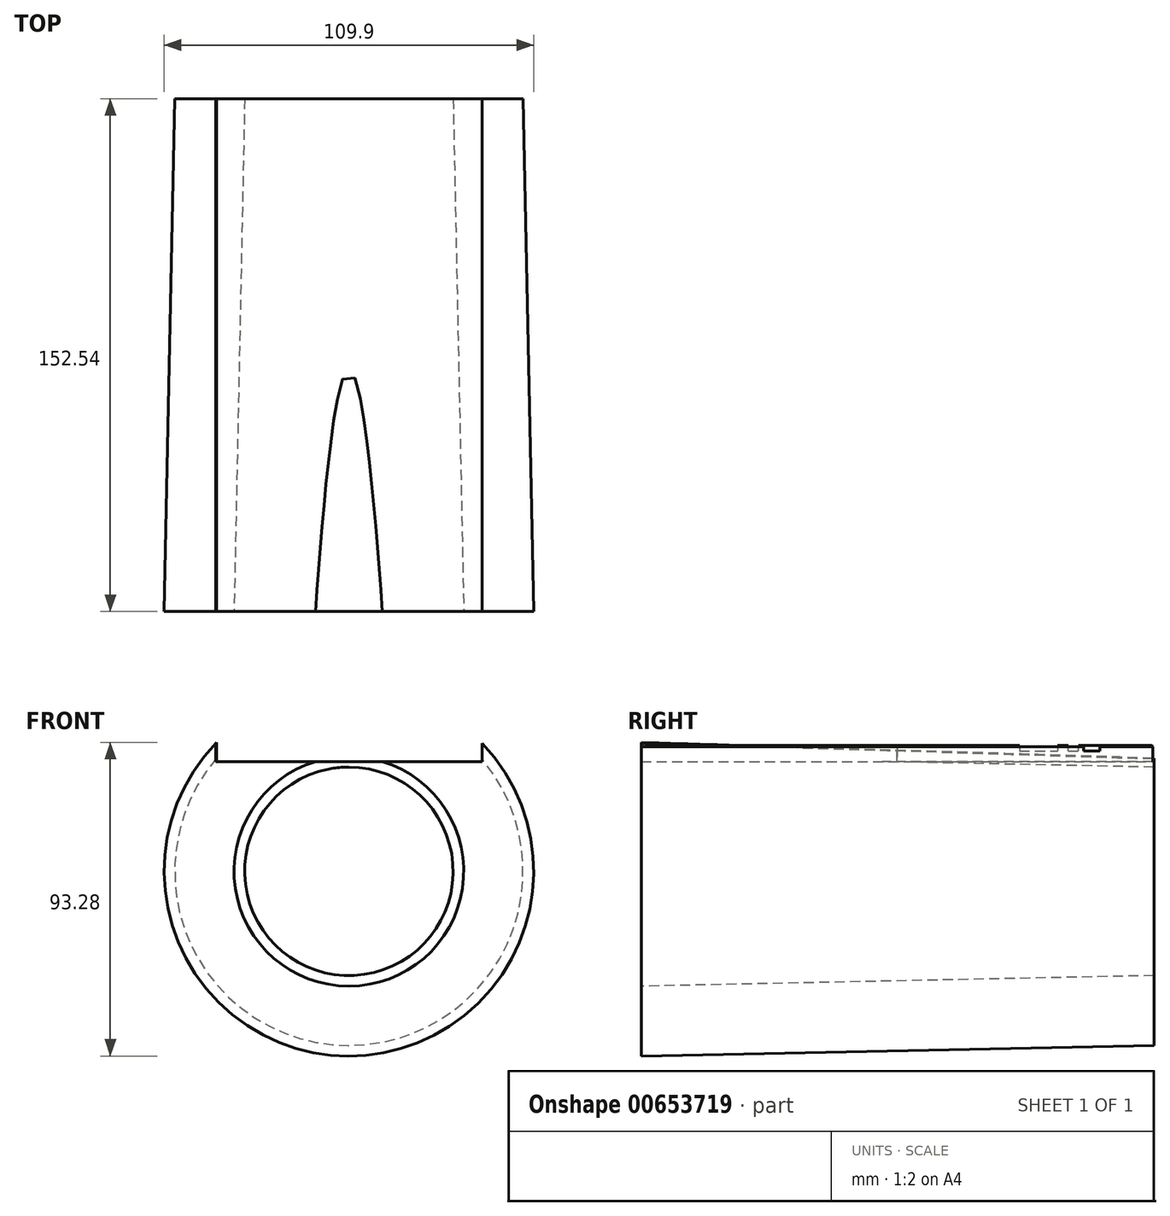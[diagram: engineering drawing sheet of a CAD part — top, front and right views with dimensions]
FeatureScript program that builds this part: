
annotation { "Feature Type Name" : "Feature", "Feature Type Description" : "" }
export const myFeature = defineFeature(function(context is Context, id is Id, definition is map)
    precondition{}
    {
        {
            var Q0;
            Q0=qCreatedBy(makeId("Top.planeOp"),FACE);
            var sketch = newSketch(context, id + "F0", { "sketchPlane" : qUnion([Q0])});
            skLineSegment(sketch, "E0.bottom", {"start": v(-25.4, 66.66) * mm, "end": v(-15.87, 66.66) * mm});
            skLineSegment(sketch, "E0.top", {"start": v(-26.98, 62.7) * mm, "end": v(-17.45, 62.7) * mm});
            skLineSegment(sketch, "E0.left", {"start": v(-26.98, 65.07) * mm, "end": v(-26.98, 62.7) * mm});
            skLineSegment(sketch, "E0.right", {"start": v(-15.87, 66.66) * mm, "end": v(-15.87, 64.28) * mm});
            skArc(sketch, "E1.filletArc", {"start": v(-25.4, 66.66) * mm, "mid": v(-26.51, 66.2) * mm, "end": v(-26.98, 65.07) * mm});
            skArc(sketch, "E2.filletArc", {"start": v(-17.45, 62.7) * mm, "mid": v(-16.33, 63.16) * mm, "end": v(-15.87, 64.28) * mm});
            skLineSegment(sketch, "E3.bottom", {"start": v(-34.92, 50.83) * mm, "end": v(-33.34, 50.83) * mm});
            skLineSegment(sketch, "E3.top", {"start": v(-34.92, 54) * mm, "end": v(-33.34, 54) * mm});
            skLineSegment(sketch, "E4.bottom", {"start": v(-34.92, 47.66) * mm, "end": v(-33.34, 47.66) * mm});
            skLineSegment(sketch, "E4.top", {"start": v(-34.92, 36.55) * mm, "end": v(-33.34, 36.55) * mm});
            skLineSegment(sketch, "E5.bottom", {"start": v(34.92, 60.29) * mm, "end": v(33.33, 60.29) * mm});
            skLineSegment(sketch, "E5.top", {"start": v(34.92, 55.52) * mm, "end": v(33.33, 55.52) * mm});
            skLineSegment(sketch, "E6.bottom", {"start": v(26.99, -69.85) * mm, "end": v(-26.99, -69.85) * mm});
            skLineSegment(sketch, "E6.top", {"start": v(26.99, 69.85) * mm, "end": v(-26.99, 69.85) * mm});
            skLineSegment(sketch, "E6.left", {"start": v(33.34, -63.5) * mm, "end": v(33.34, 63.5) * mm});
            skLineSegment(sketch, "E6.right", {"start": v(-33.34, -63.5) * mm, "end": v(-33.34, 63.5) * mm});
            skPoint(sketch, "E6.middle", {"position": v(0, 0) * mm});
            skLineSegment(sketch, "E7.bottom", {"start": v(28.57, 71.42) * mm, "end": v(-28.57, 71.42) * mm});
            skLineSegment(sketch, "E7.top", {"start": v(28.57, -71.42) * mm, "end": v(-28.57, -71.42) * mm});
            skLineSegment(sketch, "E7.left", {"start": v(34.92, 65.07) * mm, "end": v(34.92, -65.07) * mm});
            skLineSegment(sketch, "E7.right", {"start": v(-34.92, 65.07) * mm, "end": v(-34.92, -65.07) * mm});
            skLineSegment(sketch, "E8.bottom", {"start": v(24.6, -67.47) * mm, "end": v(-24.6, -67.47) * mm});
            skLineSegment(sketch, "E8.top", {"start": v(24.6, 67.47) * mm, "end": v(-24.6, 67.47) * mm});
            skLineSegment(sketch, "E8.left", {"start": v(30.96, -61.12) * mm, "end": v(30.96, 61.12) * mm});
            skLineSegment(sketch, "E8.right", {"start": v(-30.96, -61.12) * mm, "end": v(-30.96, 61.12) * mm});
            skPoint(sketch, "E9.visualSharp", {"position": v(-30.96, -67.47) * mm});
            skPoint(sketch, "E10.visualSharp", {"position": v(30.96, -67.47) * mm});
            skPoint(sketch, "E11.visualSharp", {"position": v(33.34, -69.85) * mm});
            skPoint(sketch, "E12.visualSharp", {"position": v(-33.34, -69.85) * mm});
            skPoint(sketch, "E13.visualSharp", {"position": v(-34.92, -71.42) * mm});
            skPoint(sketch, "E14.visualSharp", {"position": v(34.92, -71.42) * mm});
            skPoint(sketch, "E15.visualSharp", {"position": v(-34.92, 71.42) * mm});
            skPoint(sketch, "E16.visualSharp", {"position": v(-33.34, 69.85) * mm});
            skPoint(sketch, "E17.visualSharp", {"position": v(-30.96, 67.47) * mm});
            skPoint(sketch, "E18.visualSharp", {"position": v(30.96, 67.47) * mm});
            skPoint(sketch, "E19.visualSharp", {"position": v(33.34, 69.85) * mm});
            skPoint(sketch, "E20.visualSharp", {"position": v(34.92, 71.42) * mm});
            skLineSegment(sketch, "E21", {"start": v(-28.57, -71.42) * mm, "end": v(28.57, -71.42) * mm});
            skLineSegment(sketch, "E22.bottom", {"start": v(-25.4, -71.42) * mm, "end": v(-9.52, -71.42) * mm});
            skLineSegment(sketch, "E22.top", {"start": v(-25.4, -69.85) * mm, "end": v(-9.52, -69.85) * mm});
            skLineSegment(sketch, "E22.left", {"start": v(-25.4, -71.42) * mm, "end": v(-25.4, -69.85) * mm});
            skLineSegment(sketch, "E22.right", {"start": v(-9.52, -71.42) * mm, "end": v(-9.52, -69.85) * mm});
            skLineSegment(sketch, "E23.bottom", {"start": v(-4.76, -71.42) * mm, "end": v(6.36, -71.42) * mm});
            skLineSegment(sketch, "E23.top", {"start": v(-4.76, -69.85) * mm, "end": v(6.36, -69.85) * mm});
            skLineSegment(sketch, "E23.left", {"start": v(-4.76, -71.42) * mm, "end": v(-4.76, -69.85) * mm});
            skLineSegment(sketch, "E23.right", {"start": v(6.36, -71.42) * mm, "end": v(6.36, -69.85) * mm});
            skLineSegment(sketch, "E24", {"start": v(-28.57, -71.42) * mm, "end": v(12.42, -71.42) * mm});
            skLineSegment(sketch, "E25", {"start": v(-28.57, -71.42) * mm, "end": v(11.12, -71.42) * mm});
            skLineSegment(sketch, "E26.bottom", {"start": v(11.12, -71.42) * mm, "end": v(27.4, -71.42) * mm});
            skLineSegment(sketch, "E26.top", {"start": v(11.12, -69.85) * mm, "end": v(27.4, -69.85) * mm});
            skLineSegment(sketch, "E26.left", {"start": v(11.12, -71.42) * mm, "end": v(11.12, -69.85) * mm});
            skLineSegment(sketch, "E26.right", {"start": v(27.4, -71.42) * mm, "end": v(27.4, -69.85) * mm});
            skLineSegment(sketch, "E27", {"start": v(-24.6, -67.47) * mm, "end": v(24.6, -67.47) * mm});
            skLineSegment(sketch, "E28", {"start": v(-33.34, 63.5) * mm, "end": v(-33.34, -63.5) * mm});
            skLineSegment(sketch, "E29", {"start": v(-26.99, -69.85) * mm, "end": v(27.4, -69.85) * mm});
            skLineSegment(sketch, "E30", {"start": v(33.34, -69.85) * mm, "end": v(33.34, -69.27) * mm});
            skLineSegment(sketch, "E31", {"start": v(-28.57, 71.42) * mm, "end": v(28.57, 71.42) * mm});
            skLineSegment(sketch, "E32", {"start": v(34.92, -65.07) * mm, "end": v(34.92, 65.07) * mm});
            skLineSegment(sketch, "E33", {"start": v(-34.92, -65.07) * mm, "end": v(-34.92, 65.07) * mm});
            skArc(sketch, "E34.filletArc", {"start": v(-30.96, -61.12) * mm, "mid": v(-29.1, -65.6) * mm, "end": v(-24.6, -67.47) * mm});
            skArc(sketch, "E35.filletArc", {"start": v(-33.34, -63.5) * mm, "mid": v(-31.48, -68) * mm, "end": v(-26.99, -69.85) * mm});
            skArc(sketch, "E36.filletArc", {"start": v(-34.92, -65.07) * mm, "mid": v(-33.06, -69.56) * mm, "end": v(-28.57, -71.42) * mm});
            skArc(sketch, "E37.filletArc", {"start": v(28.57, -71.42) * mm, "mid": v(33.06, -69.56) * mm, "end": v(34.92, -65.07) * mm});
            skArc(sketch, "E38.filletArc", {"start": v(26.99, -69.85) * mm, "mid": v(31.48, -68) * mm, "end": v(33.34, -63.5) * mm});
            skArc(sketch, "E39.filletArc", {"start": v(24.6, -67.47) * mm, "mid": v(29.1, -65.6) * mm, "end": v(30.96, -61.12) * mm});
            skArc(sketch, "E40.filletArc", {"start": v(-24.6, 67.47) * mm, "mid": v(-29.1, 65.6) * mm, "end": v(-30.96, 61.12) * mm});
            skArc(sketch, "E41.filletArc", {"start": v(-26.99, 69.85) * mm, "mid": v(-31.48, 68) * mm, "end": v(-33.34, 63.5) * mm});
            skArc(sketch, "E42.filletArc", {"start": v(-28.57, 71.42) * mm, "mid": v(-33.06, 69.56) * mm, "end": v(-34.92, 65.07) * mm});
            skArc(sketch, "E43.filletArc", {"start": v(34.92, 65.07) * mm, "mid": v(33.06, 69.56) * mm, "end": v(28.57, 71.42) * mm});
            skArc(sketch, "E44.filletArc", {"start": v(33.34, 63.5) * mm, "mid": v(31.48, 68) * mm, "end": v(26.99, 69.85) * mm});
            skArc(sketch, "E45.filletArc", {"start": v(30.96, 61.12) * mm, "mid": v(29.1, 65.6) * mm, "end": v(24.6, 67.47) * mm});
            skLineSegment(sketch, "E46.trimOffspring", {"start": v(32.75, -69.85) * mm, "end": v(33.34, -69.85) * mm});
            skSolve(sketch);
        }
        {
            var Q0;
            Q0=makeQuery(id+"F0.imprint","IMPRINT",FACE,{"disambiguationData":[TD([[makeQuery(id+"F0.imprint","IMPRINT",EDGE,{"derivedFrom":sQuery(id+"F0.wireOp",EDGE,"E0.bottom")}),1.0]])]});
            var Q1;
            Q1=makeQuery(id+"F0.imprint","IMPRINT",FACE,{"disambiguationData":[TD([[makeQuery(id+"F0.imprint","IMPRINT",EDGE,{"derivedFrom":sQuery(id+"F0.wireOp",EDGE,"E8.right")}),1.0]])]});
            var Q2;
            {var subQ0=sQuery(id+"F0.wireOp",EDGE,"E28");var subQ1=sQuery(id+"F0.wireOp",EDGE,"E3.bottom");var subQ2=makeQuery(id+"F0.imprint","INTERSECT",VERTEX,{"derivedFrom":[subQ1,subQ0]});Q2=makeQuery(id+"F0.imprint","IMPRINT",FACE,{"disambiguationData":[TD([[makeQuery(id+"F0.imprint","IMPRINT",EDGE,{"disambiguationData":[TD([[subQ2,1.0]])],"derivedFrom":subQ1}),1.0]])]});}
            var Q3;
            {var subQ0=sQuery(id+"F0.wireOp",EDGE,"E28");var subQ1=sQuery(id+"F0.wireOp",EDGE,"E3.bottom");var subQ2=makeQuery(id+"F0.imprint","INTERSECT",VERTEX,{"derivedFrom":[subQ1,subQ0]});Q3=makeQuery(id+"F0.imprint","IMPRINT",FACE,{"disambiguationData":[TD([[makeQuery(id+"F0.imprint","IMPRINT",EDGE,{"disambiguationData":[TD([[subQ2,1.0]])],"derivedFrom":subQ1}),-1.0]])]});}
            var Q4;
            {var subQ0=sQuery(id+"F0.wireOp",EDGE,"E28");var subQ1=sQuery(id+"F0.wireOp",EDGE,"E4.bottom");var subQ2=makeQuery(id+"F0.imprint","INTERSECT",VERTEX,{"derivedFrom":[subQ1,subQ0]});Q4=makeQuery(id+"F0.imprint","IMPRINT",FACE,{"disambiguationData":[TD([[makeQuery(id+"F0.imprint","IMPRINT",EDGE,{"disambiguationData":[TD([[subQ2,1.0]])],"derivedFrom":subQ1}),-1.0]])]});}
            var Q5;
            Q5=makeQuery(id+"F0.imprint","IMPRINT",FACE,{"disambiguationData":[TD([[makeQuery(id+"F0.imprint","IMPRINT",EDGE,{"derivedFrom":sQuery(id+"F0.wireOp",EDGE,"E6.top")}),-1.0]])]});
            var Q6;
            {var subQ5=sQuery(id+"F0.wireOp",EDGE,"E22.left");Q6=makeQuery(id+"F0.imprint","IMPRINT",FACE,{"disambiguationData":[TD([[makeQuery(id+"F0.imprint","IMPRINT",EDGE,{"derivedFrom":subQ5}),1.0]])]});}
            var Q7;
            {var subQ0=sQuery(id+"F0.wireOp",EDGE,"E32");var subQ1=sQuery(id+"F0.wireOp",EDGE,"E5.bottom");var subQ2=makeQuery(id+"F0.imprint","INTERSECT",VERTEX,{"derivedFrom":[subQ1,subQ0]});Q7=makeQuery(id+"F0.imprint","IMPRINT",FACE,{"disambiguationData":[TD([[makeQuery(id+"F0.imprint","IMPRINT",EDGE,{"disambiguationData":[TD([[subQ2,-1.0]])],"derivedFrom":subQ1}),1.0]])]});}
            var Q8;
            {var subQ3=sQuery(id+"F0.wireOp",EDGE,"E21");Q8=makeQuery(id+"F0.imprint","IMPRINT",FACE,{"disambiguationData":[TD([[makeQuery(id+"F0.imprint","IMPRINT",EDGE,{"derivedFrom":subQ3}),1.0]])]});}
            var Q9;
            {var subQ2=sQuery(id+"F0.wireOp",EDGE,"E26.left");Q9=makeQuery(id+"F0.imprint","IMPRINT",FACE,{"disambiguationData":[TD([[makeQuery(id+"F0.imprint","IMPRINT",EDGE,{"derivedFrom":subQ2}),-1.0]])]});}
            var Q10;
            {var subQ0=sQuery(id+"F0.wireOp",EDGE,"E23.right");Q10=makeQuery(id+"F0.imprint","IMPRINT",FACE,{"disambiguationData":[TD([[makeQuery(id+"F0.imprint","IMPRINT",EDGE,{"derivedFrom":subQ0}),-1.0]])]});}
            var Q11;
            {var subQ0=sQuery(id+"F0.wireOp",EDGE,"E23.left");Q11=makeQuery(id+"F0.imprint","IMPRINT",FACE,{"disambiguationData":[TD([[makeQuery(id+"F0.imprint","IMPRINT",EDGE,{"derivedFrom":subQ0}),-1.0]])]});}
            var Q12;
            {var subQ0=sQuery(id+"F0.wireOp",EDGE,"E22.right");Q12=makeQuery(id+"F0.imprint","IMPRINT",FACE,{"disambiguationData":[TD([[makeQuery(id+"F0.imprint","IMPRINT",EDGE,{"derivedFrom":subQ0}),-1.0]])]});}
            var Q13;
            {var subQ0=sQuery(id+"F0.wireOp",EDGE,"E22.left");Q13=makeQuery(id+"F0.imprint","IMPRINT",FACE,{"disambiguationData":[TD([[makeQuery(id+"F0.imprint","IMPRINT",EDGE,{"derivedFrom":subQ0}),-1.0]])]});}
            extrude(context, id + "F1", {"entities" : qUnion([Q0, Q1, Q2, Q3, Q4, Q5, Q6, Q7, Q8, Q9, Q10, Q11, Q12, Q13]), "depth" : 3.17 * mm, "offsetDistance" : 25.4 * mm});
        }
        {
            var Q0;
            {var subQ5=sQuery(id+"F0.wireOp",EDGE,"E22.left");Q0=makeQuery(id+"F0.imprint","IMPRINT",FACE,{"disambiguationData":[TD([[makeQuery(id+"F0.imprint","IMPRINT",EDGE,{"derivedFrom":subQ5}),1.0]])]});}
            var Q1;
            {var subQ0=sQuery(id+"F0.wireOp",EDGE,"E28");var subQ1=sQuery(id+"F0.wireOp",EDGE,"E3.bottom");var subQ2=makeQuery(id+"F0.imprint","INTERSECT",VERTEX,{"derivedFrom":[subQ1,subQ0]});Q1=makeQuery(id+"F0.imprint","IMPRINT",FACE,{"disambiguationData":[TD([[makeQuery(id+"F0.imprint","IMPRINT",EDGE,{"disambiguationData":[TD([[subQ2,1.0]])],"derivedFrom":subQ1}),-1.0]])]});}
            var Q2;
            Q2=makeQuery(id+"F0.imprint","IMPRINT",FACE,{"disambiguationData":[TD([[makeQuery(id+"F0.imprint","IMPRINT",EDGE,{"derivedFrom":sQuery(id+"F0.wireOp",EDGE,"E6.top")}),-1.0]])]});
            var Q3;
            {var subQ3=sQuery(id+"F0.wireOp",EDGE,"E21");Q3=makeQuery(id+"F0.imprint","IMPRINT",FACE,{"disambiguationData":[TD([[makeQuery(id+"F0.imprint","IMPRINT",EDGE,{"derivedFrom":subQ3}),1.0]])]});}
            var Q4;
            {var subQ0=sQuery(id+"F0.wireOp",EDGE,"E22.right");Q4=makeQuery(id+"F0.imprint","IMPRINT",FACE,{"disambiguationData":[TD([[makeQuery(id+"F0.imprint","IMPRINT",EDGE,{"derivedFrom":subQ0}),-1.0]])]});}
            var Q5;
            {var subQ0=sQuery(id+"F0.wireOp",EDGE,"E23.right");Q5=makeQuery(id+"F0.imprint","IMPRINT",FACE,{"disambiguationData":[TD([[makeQuery(id+"F0.imprint","IMPRINT",EDGE,{"derivedFrom":subQ0}),-1.0]])]});}
            extrude(context, id + "F2", {"entities" : qUnion([Q0, Q1, Q2, Q3, Q4, Q5]), "operationType" : NewBodyOperationType.ADD, "depth" : 9.52 * mm, "offsetDistance" : 25.4 * mm});
        }
        {
            var Q0;
            Q0=makeQuery(id+"F0.imprint","IMPRINT",FACE,{"disambiguationData":[TD([[makeQuery(id+"F0.imprint","IMPRINT",EDGE,{"derivedFrom":sQuery(id+"F0.wireOp",EDGE,"E8.right")}),1.0]])]});
            var Q1;
            {var subQ0=sQuery(id+"F0.wireOp",EDGE,"E28");var subQ1=sQuery(id+"F0.wireOp",EDGE,"E4.bottom");var subQ2=makeQuery(id+"F0.imprint","INTERSECT",VERTEX,{"derivedFrom":[subQ1,subQ0]});Q1=makeQuery(id+"F0.imprint","IMPRINT",FACE,{"disambiguationData":[TD([[makeQuery(id+"F0.imprint","IMPRINT",EDGE,{"disambiguationData":[TD([[subQ2,1.0]])],"derivedFrom":subQ1}),-1.0]])]});}
            var Q2;
            {var subQ0=sQuery(id+"F0.wireOp",EDGE,"E28");var subQ1=sQuery(id+"F0.wireOp",EDGE,"E3.bottom");var subQ2=makeQuery(id+"F0.imprint","INTERSECT",VERTEX,{"derivedFrom":[subQ1,subQ0]});Q2=makeQuery(id+"F0.imprint","IMPRINT",FACE,{"disambiguationData":[TD([[makeQuery(id+"F0.imprint","IMPRINT",EDGE,{"disambiguationData":[TD([[subQ2,1.0]])],"derivedFrom":subQ1}),-1.0]])]});}
            var Q3;
            {var subQ0=sQuery(id+"F0.wireOp",EDGE,"E28");var subQ1=sQuery(id+"F0.wireOp",EDGE,"E3.bottom");var subQ2=makeQuery(id+"F0.imprint","INTERSECT",VERTEX,{"derivedFrom":[subQ1,subQ0]});Q3=makeQuery(id+"F0.imprint","IMPRINT",FACE,{"disambiguationData":[TD([[makeQuery(id+"F0.imprint","IMPRINT",EDGE,{"disambiguationData":[TD([[subQ2,1.0]])],"derivedFrom":subQ1}),1.0]])]});}
            var Q4;
            Q4=makeQuery(id+"F0.imprint","IMPRINT",FACE,{"disambiguationData":[TD([[makeQuery(id+"F0.imprint","IMPRINT",EDGE,{"derivedFrom":sQuery(id+"F0.wireOp",EDGE,"E6.top")}),-1.0]])]});
            var Q5;
            {var subQ5=sQuery(id+"F0.wireOp",EDGE,"E22.left");Q5=makeQuery(id+"F0.imprint","IMPRINT",FACE,{"disambiguationData":[TD([[makeQuery(id+"F0.imprint","IMPRINT",EDGE,{"derivedFrom":subQ5}),1.0]])]});}
            var Q6;
            {var subQ0=sQuery(id+"F0.wireOp",EDGE,"E32");var subQ1=sQuery(id+"F0.wireOp",EDGE,"E5.bottom");var subQ2=makeQuery(id+"F0.imprint","INTERSECT",VERTEX,{"derivedFrom":[subQ1,subQ0]});Q6=makeQuery(id+"F0.imprint","IMPRINT",FACE,{"disambiguationData":[TD([[makeQuery(id+"F0.imprint","IMPRINT",EDGE,{"disambiguationData":[TD([[subQ2,-1.0]])],"derivedFrom":subQ1}),1.0]])]});}
            var Q7;
            {var subQ3=sQuery(id+"F0.wireOp",EDGE,"E21");Q7=makeQuery(id+"F0.imprint","IMPRINT",FACE,{"disambiguationData":[TD([[makeQuery(id+"F0.imprint","IMPRINT",EDGE,{"derivedFrom":subQ3}),1.0]])]});}
            var Q8;
            {var subQ0=sQuery(id+"F0.wireOp",EDGE,"E22.left");Q8=makeQuery(id+"F0.imprint","IMPRINT",FACE,{"disambiguationData":[TD([[makeQuery(id+"F0.imprint","IMPRINT",EDGE,{"derivedFrom":subQ0}),-1.0]])]});}
            var Q9;
            {var subQ0=sQuery(id+"F0.wireOp",EDGE,"E22.right");Q9=makeQuery(id+"F0.imprint","IMPRINT",FACE,{"disambiguationData":[TD([[makeQuery(id+"F0.imprint","IMPRINT",EDGE,{"derivedFrom":subQ0}),-1.0]])]});}
            var Q10;
            {var subQ0=sQuery(id+"F0.wireOp",EDGE,"E23.left");Q10=makeQuery(id+"F0.imprint","IMPRINT",FACE,{"disambiguationData":[TD([[makeQuery(id+"F0.imprint","IMPRINT",EDGE,{"derivedFrom":subQ0}),-1.0]])]});}
            var Q11;
            {var subQ0=sQuery(id+"F0.wireOp",EDGE,"E23.right");Q11=makeQuery(id+"F0.imprint","IMPRINT",FACE,{"disambiguationData":[TD([[makeQuery(id+"F0.imprint","IMPRINT",EDGE,{"derivedFrom":subQ0}),-1.0]])]});}
            var Q12;
            {var subQ2=sQuery(id+"F0.wireOp",EDGE,"E26.left");Q12=makeQuery(id+"F0.imprint","IMPRINT",FACE,{"disambiguationData":[TD([[makeQuery(id+"F0.imprint","IMPRINT",EDGE,{"derivedFrom":subQ2}),-1.0]])]});}
            extrude(context, id + "F3", {"entities" : qUnion([Q0, Q1, Q2, Q3, Q4, Q5, Q6, Q7, Q8, Q9, Q10, Q11, Q12]), "depth" : 12.7 * mm, "offsetDistance" : 25.4 * mm, "hasSecondDirection" : true, "secondDirectionOppositeDirection" : false, "secondDirectionDepth" : 9.52 * mm});
        }
        {
            var Q0;
            Q0=makeQuery(id+"F3.opExtrude","CAP_EDGE",EDGE,{"disambiguationData":[OSD([sQuery(id+"F0.wireOp",EDGE,"E32")])],"isStart":false});
            var Q1;
            Q1=makeQuery(id+"F3.opExtrude","CAP_EDGE",EDGE,{"disambiguationData":[OSD([sQuery(id+"F0.wireOp",EDGE,"E37.filletArc")])],"isStart":false});
            var Q2;
            Q2=makeQuery(id+"F3.opExtrude","CAP_EDGE",EDGE,{"disambiguationData":[OSD([sQuery(id+"F0.wireOp",EDGE,"E21"),sQuery(id+"F0.wireOp",EDGE,"E25"),sQuery(id+"F0.wireOp",EDGE,"E26.bottom")])],"isStart":false});
            var Q3;
            Q3=makeQuery(id+"F3.opExtrude","CAP_EDGE",EDGE,{"disambiguationData":[OSD([sQuery(id+"F0.wireOp",EDGE,"E36.filletArc")])],"isStart":false});
            var Q4;
            Q4=makeQuery(id+"F3.opExtrude","CAP_EDGE",EDGE,{"disambiguationData":[OSD([sQuery(id+"F0.wireOp",EDGE,"E33")])],"isStart":false});
            var Q5;
            Q5=makeQuery(id+"F3.opExtrude","CAP_EDGE",EDGE,{"disambiguationData":[OSD([sQuery(id+"F0.wireOp",EDGE,"E42.filletArc")])],"isStart":false});
            var Q6;
            Q6=makeQuery(id+"F3.opExtrude","CAP_EDGE",EDGE,{"disambiguationData":[OSD([sQuery(id+"F0.wireOp",EDGE,"E31")])],"isStart":false});
            var Q7;
            Q7=makeQuery(id+"F3.opExtrude","CAP_EDGE",EDGE,{"disambiguationData":[OSD([sQuery(id+"F0.wireOp",EDGE,"E43.filletArc")])],"isStart":false});
            fillet(context, id + "F4", {"entities" : qUnion([Q0, Q1, Q2, Q3, Q4, Q5, Q6, Q7]), "radius" : 5.08 * mm, "tangentPropagation" : true, "allowEdgeOverflow" : false});
        }
        {
            var Q0;
            Q0=makeQuery(id+"F1.opExtrude","CAP_EDGE",EDGE,{"disambiguationData":[OSD([sQuery(id+"F0.wireOp",EDGE,"E33")])],"isStart":true});
            var Q1;
            Q1=makeQuery(id+"F1.opExtrude","CAP_EDGE",EDGE,{"disambiguationData":[OSD([sQuery(id+"F0.wireOp",EDGE,"E42.filletArc")])],"isStart":true});
            var Q2;
            Q2=makeQuery(id+"F1.opExtrude","CAP_EDGE",EDGE,{"disambiguationData":[OSD([sQuery(id+"F0.wireOp",EDGE,"E31")])],"isStart":true});
            var Q3;
            Q3=makeQuery(id+"F1.opExtrude","CAP_EDGE",EDGE,{"disambiguationData":[OSD([sQuery(id+"F0.wireOp",EDGE,"E43.filletArc")])],"isStart":true});
            var Q4;
            Q4=makeQuery(id+"F1.opExtrude","CAP_EDGE",EDGE,{"disambiguationData":[OSD([sQuery(id+"F0.wireOp",EDGE,"E32")])],"isStart":true});
            var Q5;
            Q5=makeQuery(id+"F1.opExtrude","CAP_EDGE",EDGE,{"disambiguationData":[OSD([sQuery(id+"F0.wireOp",EDGE,"E36.filletArc")])],"isStart":true});
            var Q6;
            Q6=makeQuery(id+"F1.opExtrude","CAP_EDGE",EDGE,{"disambiguationData":[OSD([sQuery(id+"F0.wireOp",EDGE,"E21"),sQuery(id+"F0.wireOp",EDGE,"E25"),sQuery(id+"F0.wireOp",EDGE,"E26.bottom")])],"isStart":true});
            var Q7;
            Q7=makeQuery(id+"F1.opExtrude","CAP_EDGE",EDGE,{"disambiguationData":[OSD([sQuery(id+"F0.wireOp",EDGE,"E37.filletArc")])],"isStart":true});
            fillet(context, id + "F5", {"entities" : qUnion([Q0, Q1, Q2, Q3, Q4, Q5, Q6, Q7]), "radius" : 5.08 * mm, "tangentPropagation" : true, "allowEdgeOverflow" : false});
        }
        {
            var Q0;
            Q0=qCreatedBy(makeId("Right.planeOp"),FACE);
            var sketch = newSketch(context, id + "F6", { "sketchPlane" : qUnion([Q0])});
            skLineSegment(sketch, "E47.bottom", {"start": v(54.03, 9.64) * mm, "end": v(50.87, 9.64) * mm});
            skLineSegment(sketch, "E47.top", {"start": v(54.03, 3.18) * mm, "end": v(50.87, 3.18) * mm});
            skLineSegment(sketch, "E47.left", {"start": v(54.03, 9.64) * mm, "end": v(54.03, 3.18) * mm});
            skLineSegment(sketch, "E47.right", {"start": v(50.87, 9.64) * mm, "end": v(50.87, 3.18) * mm});
            skLineSegment(sketch, "E48.bottom", {"start": v(47.79, 3.18) * mm, "end": v(36.43, 3.18) * mm});
            skLineSegment(sketch, "E48.top", {"start": v(47.79, 9.64) * mm, "end": v(36.43, 9.64) * mm});
            skLineSegment(sketch, "E48.left", {"start": v(47.79, 3.18) * mm, "end": v(47.79, 9.64) * mm});
            skLineSegment(sketch, "E48.right", {"start": v(36.43, 3.18) * mm, "end": v(36.43, 9.64) * mm});
            skSolve(sketch);
        }
        {
            var Q0;
            Q0=qCreatedBy(makeId("Right.planeOp"),FACE);
            var sketch = newSketch(context, id + "F7", { "sketchPlane" : qUnion([Q0])});
            skLineSegment(sketch, "E49.bottom", {"start": v(55.5, 9.63) * mm, "end": v(60.3, 9.63) * mm});
            skLineSegment(sketch, "E49.top", {"start": v(55.5, 3.16) * mm, "end": v(60.3, 3.16) * mm});
            skLineSegment(sketch, "E49.left", {"start": v(55.5, 9.63) * mm, "end": v(55.5, 3.16) * mm});
            skLineSegment(sketch, "E49.right", {"start": v(60.3, 9.63) * mm, "end": v(60.3, 3.16) * mm});
            skSolve(sketch);
        }
        {
            var Q0;
            Q0=qCreatedBy(makeId("Front.planeOp"),FACE);
            var sketch = newSketch(context, id + "F8", { "sketchPlane" : qUnion([Q0])});
            skLineSegment(sketch, "E50.bottom", {"start": v(-25.46, 9.6) * mm, "end": v(-9.52, 9.6) * mm});
            skLineSegment(sketch, "E50.top", {"start": v(-25.46, 3.13) * mm, "end": v(-9.52, 3.13) * mm});
            skLineSegment(sketch, "E50.left", {"start": v(-25.46, 9.6) * mm, "end": v(-25.46, 3.13) * mm});
            skLineSegment(sketch, "E50.right", {"start": v(-9.52, 9.6) * mm, "end": v(-9.52, 3.13) * mm});
            skLineSegment(sketch, "E51.bottom", {"start": v(-4.78, 3.13) * mm, "end": v(6.35, 3.13) * mm});
            skLineSegment(sketch, "E51.top", {"start": v(-4.78, 9.52) * mm, "end": v(6.35, 9.52) * mm});
            skLineSegment(sketch, "E51.left", {"start": v(-4.78, 3.13) * mm, "end": v(-4.78, 9.52) * mm});
            skLineSegment(sketch, "E51.right", {"start": v(6.35, 3.13) * mm, "end": v(6.35, 9.52) * mm});
            skLineSegment(sketch, "E52.bottom", {"start": v(11.09, 9.52) * mm, "end": v(27.33, 9.52) * mm});
            skLineSegment(sketch, "E52.top", {"start": v(11.09, 3.13) * mm, "end": v(27.33, 3.13) * mm});
            skLineSegment(sketch, "E52.left", {"start": v(11.09, 9.52) * mm, "end": v(11.09, 3.13) * mm});
            skLineSegment(sketch, "E52.right", {"start": v(27.33, 9.52) * mm, "end": v(27.33, 3.13) * mm});
            skLineSegment(sketch, "E53", {"start": v(-31.08, 14.78) * mm, "end": v(-39.67, 4.4) * mm});
            skLineSegment(sketch, "E54", {"start": v(-39.67, 4.4) * mm, "end": v(-39.67, 0) * mm});
            skLineSegment(sketch, "E55", {"start": v(-39.67, 0) * mm, "end": v(0, 0) * mm});
            skLineSegment(sketch, "E56.MirrorCS", {"start": v(31.08, 14.78) * mm, "end": v(39.67, 4.4) * mm});
            skLineSegment(sketch, "E57.MirrorCS", {"start": v(39.67, 0) * mm, "end": v(0, 0) * mm});
            skLineSegment(sketch, "E58.MirrorCS", {"start": v(39.67, 4.4) * mm, "end": v(39.67, 0) * mm});
            skLineSegment(sketch, "E59", {"start": v(-31.08, 14.78) * mm, "end": v(31.08, 14.78) * mm});
            skSolve(sketch);
        }
        {
            var Q0;
            Q0=qCreatedBy(makeId("Right.planeOp"),FACE);
            var sketch = newSketch(context, id + "F9", { "sketchPlane" : qUnion([Q0])});
            skLineSegment(sketch, "E60", {"start": v(-67.54, 14.78) * mm, "end": v(-76.12, 4.4) * mm});
            skLineSegment(sketch, "E61", {"start": v(-76.12, 4.4) * mm, "end": v(-76.12, 0) * mm});
            skLineSegment(sketch, "E62", {"start": v(-76.12, 0) * mm, "end": v(0, 0) * mm});
            skLineSegment(sketch, "E63.MirrorCS", {"start": v(76.12, 0) * mm, "end": v(0, 0) * mm});
            skLineSegment(sketch, "E64.MirrorCS", {"start": v(67.54, 14.78) * mm, "end": v(76.12, 4.4) * mm});
            skLineSegment(sketch, "E65.MirrorCS", {"start": v(76.12, 4.4) * mm, "end": v(76.12, 0) * mm});
            skLineSegment(sketch, "E66", {"start": v(-67.54, 14.78) * mm, "end": v(67.54, 14.78) * mm});
            skLineSegment(sketch, "E67.bottom", {"start": v(54.16, 9.74) * mm, "end": v(50.62, 9.74) * mm});
            skLineSegment(sketch, "E67.top", {"start": v(54.16, 2.79) * mm, "end": v(50.62, 2.79) * mm});
            skLineSegment(sketch, "E67.left", {"start": v(54.16, 9.74) * mm, "end": v(54.16, 2.79) * mm});
            skLineSegment(sketch, "E67.right", {"start": v(50.62, 9.74) * mm, "end": v(50.62, 2.79) * mm});
            skLineSegment(sketch, "E68.bottom", {"start": v(47.7, 2.79) * mm, "end": v(36.45, 2.79) * mm});
            skLineSegment(sketch, "E68.top", {"start": v(47.7, 9.61) * mm, "end": v(36.45, 9.61) * mm});
            skLineSegment(sketch, "E68.left", {"start": v(47.7, 2.79) * mm, "end": v(47.7, 9.61) * mm});
            skLineSegment(sketch, "E68.right", {"start": v(36.45, 2.79) * mm, "end": v(36.45, 9.61) * mm});
            skSolve(sketch);
        }
        {
            var Q0;
            Q0=makeQuery(id+"F8.imprint","IMPRINT",FACE,{"disambiguationData":[TD([[makeQuery(id+"F8.imprint","IMPRINT",EDGE,{"derivedFrom":sQuery(id+"F8.wireOp",EDGE,"E50.bottom")}),1.0]])]});
            extrude(context, id + "F10", {"entities" : qUnion([Q0]), "depth" : 76.2 * mm, "offsetDistance" : 25.4 * mm});
        }
        {
            var Q0;
            Q0=makeQuery(id+"F9.imprint","IMPRINT",FACE,{"disambiguationData":[TD([[makeQuery(id+"F9.imprint","IMPRINT",EDGE,{"derivedFrom":sQuery(id+"F9.wireOp",EDGE,"E60")}),1.0]])]});
            extrude(context, id + "F11", {"entities" : qUnion([Q0]), "oppositeDirection" : true, "depth" : 74.42 * mm, "offsetDistance" : 25.4 * mm});
        }
        {
            var Q0;
            Q0=makeQuery(id+"F9.imprint","IMPRINT",FACE,{"disambiguationData":[TD([[makeQuery(id+"F9.imprint","IMPRINT",EDGE,{"derivedFrom":sQuery(id+"F9.wireOp",EDGE,"E60")}),1.0]])]});
            var Q1;
            Q1=makeQuery(id+"F9.imprint","IMPRINT",FACE,{"disambiguationData":[TD([[makeQuery(id+"F9.imprint","IMPRINT",EDGE,{"derivedFrom":sQuery(id+"F9.wireOp",EDGE,"E68.bottom")}),-1.0]])]});
            var Q2;
            Q2=makeQuery(id+"F9.imprint","IMPRINT",FACE,{"disambiguationData":[TD([[makeQuery(id+"F9.imprint","IMPRINT",EDGE,{"derivedFrom":sQuery(id+"F9.wireOp",EDGE,"E67.bottom")}),1.0]])]});
            extrude(context, id + "F12", {"entities" : qUnion([Q0, Q1, Q2]), "depth" : 53.1 * mm, "offsetDistance" : 25.4 * mm});
        }
        {
            var Q0;
            Q0=makeQuery(id+"F8.imprint","IMPRINT",FACE,{"disambiguationData":[TD([[makeQuery(id+"F8.imprint","IMPRINT",EDGE,{"derivedFrom":sQuery(id+"F8.wireOp",EDGE,"E51.bottom")}),1.0]])]});
            var Q1;
            Q1=makeQuery(id+"F8.imprint","IMPRINT",FACE,{"disambiguationData":[TD([[makeQuery(id+"F8.imprint","IMPRINT",EDGE,{"derivedFrom":sQuery(id+"F8.wireOp",EDGE,"E50.bottom")}),1.0]])]});
            var Q2;
            Q2=makeQuery(id+"F8.imprint","IMPRINT",FACE,{"disambiguationData":[TD([[makeQuery(id+"F8.imprint","IMPRINT",EDGE,{"derivedFrom":sQuery(id+"F8.wireOp",EDGE,"E50.bottom")}),-1.0]])]});
            var Q3;
            Q3=makeQuery(id+"F8.imprint","IMPRINT",FACE,{"disambiguationData":[TD([[makeQuery(id+"F8.imprint","IMPRINT",EDGE,{"derivedFrom":sQuery(id+"F8.wireOp",EDGE,"E52.bottom")}),-1.0]])]});
            extrude(context, id + "F13", {"entities" : qUnion([Q0, Q1, Q2, Q3]), "oppositeDirection" : true, "depth" : 127 * mm, "offsetDistance" : 25.4 * mm});
        }
        {
            var Q0;
            Q0=makeQuery(id+"F10.opExtrude","SWEPT_BODY",BODY,{"disambiguationData":[OSD([sQuery(id+"F8.wireOp",EDGE,"E50.bottom"),sQuery(id+"F8.wireOp",EDGE,"E50.top"),sQuery(id+"F8.wireOp",EDGE,"E50.left"),sQuery(id+"F8.wireOp",EDGE,"E50.right"),sQuery(id+"F8.wireOp",EDGE,"E51.bottom"),sQuery(id+"F8.wireOp",EDGE,"E51.top"),sQuery(id+"F8.wireOp",EDGE,"E51.left"),sQuery(id+"F8.wireOp",EDGE,"E51.right"),sQuery(id+"F8.wireOp",EDGE,"E52.bottom"),sQuery(id+"F8.wireOp",EDGE,"E52.top"),sQuery(id+"F8.wireOp",EDGE,"E52.left"),sQuery(id+"F8.wireOp",EDGE,"E52.right"),sQuery(id+"F8.wireOp",EDGE,"E53"),sQuery(id+"F8.wireOp",EDGE,"E54"),sQuery(id+"F8.wireOp",EDGE,"E55"),sQuery(id+"F8.wireOp",EDGE,"E56.MirrorCS"),sQuery(id+"F8.wireOp",EDGE,"E57.MirrorCS"),sQuery(id+"F8.wireOp",EDGE,"E58.MirrorCS"),sQuery(id+"F8.wireOp",EDGE,"E59")])]});
            var Q1;
            Q1=makeQuery(id+"F11.opExtrude","SWEPT_BODY",BODY,{"disambiguationData":[OSD([sQuery(id+"F9.wireOp",EDGE,"E60"),sQuery(id+"F9.wireOp",EDGE,"E61"),sQuery(id+"F9.wireOp",EDGE,"E62"),sQuery(id+"F9.wireOp",EDGE,"E63.MirrorCS"),sQuery(id+"F9.wireOp",EDGE,"E64.MirrorCS"),sQuery(id+"F9.wireOp",EDGE,"E65.MirrorCS"),sQuery(id+"F9.wireOp",EDGE,"E66"),sQuery(id+"F9.wireOp",EDGE,"E67.bottom"),sQuery(id+"F9.wireOp",EDGE,"E67.top"),sQuery(id+"F9.wireOp",EDGE,"E67.left"),sQuery(id+"F9.wireOp",EDGE,"E67.right"),sQuery(id+"F9.wireOp",EDGE,"E68.bottom"),sQuery(id+"F9.wireOp",EDGE,"E68.top"),sQuery(id+"F9.wireOp",EDGE,"E68.left"),sQuery(id+"F9.wireOp",EDGE,"E68.right")])]});
            booleanBodies(context, id + "F14", {"operationType" : BooleanOperationType.INTERSECTION, "tools" : qUnion([Q0, Q1])});
        }
        {
            var Q0;
            Q0=makeQuery(id+"F12.opExtrude","SWEPT_BODY",BODY,{"disambiguationData":[OSD([sQuery(id+"F9.wireOp",EDGE,"E60"),sQuery(id+"F9.wireOp",EDGE,"E61"),sQuery(id+"F9.wireOp",EDGE,"E62"),sQuery(id+"F9.wireOp",EDGE,"E63.MirrorCS"),sQuery(id+"F9.wireOp",EDGE,"E64.MirrorCS"),sQuery(id+"F9.wireOp",EDGE,"E65.MirrorCS"),sQuery(id+"F9.wireOp",EDGE,"E66")])]});
            var Q1;
            Q1=makeQuery(id+"F13.opExtrude","SWEPT_BODY",BODY,{"disambiguationData":[OSD([sQuery(id+"F8.wireOp",EDGE,"E53"),sQuery(id+"F8.wireOp",EDGE,"E54"),sQuery(id+"F8.wireOp",EDGE,"E55"),sQuery(id+"F8.wireOp",EDGE,"E56.MirrorCS"),sQuery(id+"F8.wireOp",EDGE,"E57.MirrorCS"),sQuery(id+"F8.wireOp",EDGE,"E58.MirrorCS"),sQuery(id+"F8.wireOp",EDGE,"E59")])]});
            booleanBodies(context, id + "F15", {"operationType" : BooleanOperationType.INTERSECTION, "tools" : qUnion([Q0, Q1])});
        }
        {
            var Q0;
            Q0=makeQuery(id+"F9.imprint","IMPRINT",FACE,{"disambiguationData":[TD([[makeQuery(id+"F9.imprint","IMPRINT",EDGE,{"derivedFrom":sQuery(id+"F9.wireOp",EDGE,"E68.bottom")}),-1.0]])]});
            var Q1;
            Q1=makeQuery(id+"F9.imprint","IMPRINT",FACE,{"disambiguationData":[TD([[makeQuery(id+"F9.imprint","IMPRINT",EDGE,{"derivedFrom":sQuery(id+"F9.wireOp",EDGE,"E67.bottom")}),1.0]])]});
            var Q2;
            Q2=makeQuery(id+"F9.imprint","IMPRINT",FACE,{"disambiguationData":[TD([[makeQuery(id+"F9.imprint","IMPRINT",EDGE,{"derivedFrom":sQuery(id+"F9.wireOp",EDGE,"E60")}),1.0]])]});
            extrude(context, id + "F16", {"entities" : qUnion([Q0, Q1, Q2]), "oppositeDirection" : true, "depth" : 63 * mm, "offsetDistance" : 25.4 * mm});
        }
        {
            var Q0;
            Q0=makeQuery(id+"F8.imprint","IMPRINT",FACE,{"disambiguationData":[TD([[makeQuery(id+"F8.imprint","IMPRINT",EDGE,{"derivedFrom":sQuery(id+"F8.wireOp",EDGE,"E51.bottom")}),1.0]])]});
            var Q1;
            Q1=makeQuery(id+"F8.imprint","IMPRINT",FACE,{"disambiguationData":[TD([[makeQuery(id+"F8.imprint","IMPRINT",EDGE,{"derivedFrom":sQuery(id+"F8.wireOp",EDGE,"E50.bottom")}),1.0]])]});
            var Q2;
            Q2=makeQuery(id+"F8.imprint","IMPRINT",FACE,{"disambiguationData":[TD([[makeQuery(id+"F8.imprint","IMPRINT",EDGE,{"derivedFrom":sQuery(id+"F8.wireOp",EDGE,"E50.bottom")}),-1.0]])]});
            var Q3;
            Q3=makeQuery(id+"F8.imprint","IMPRINT",FACE,{"disambiguationData":[TD([[makeQuery(id+"F8.imprint","IMPRINT",EDGE,{"derivedFrom":sQuery(id+"F8.wireOp",EDGE,"E52.bottom")}),-1.0]])]});
            extrude(context, id + "F17", {"entities" : qUnion([Q0, Q1, Q2, Q3]), "oppositeDirection" : true, "depth" : 137.67 * mm, "offsetDistance" : 25.4 * mm});
        }
        {
            var Q0;
            Q0=makeQuery(id+"F16.opExtrude","SWEPT_BODY",BODY,{"disambiguationData":[OSD([sQuery(id+"F9.wireOp",EDGE,"E60"),sQuery(id+"F9.wireOp",EDGE,"E61"),sQuery(id+"F9.wireOp",EDGE,"E62"),sQuery(id+"F9.wireOp",EDGE,"E63.MirrorCS"),sQuery(id+"F9.wireOp",EDGE,"E64.MirrorCS"),sQuery(id+"F9.wireOp",EDGE,"E65.MirrorCS"),sQuery(id+"F9.wireOp",EDGE,"E66")])]});
            var Q1;
            Q1=makeQuery(id+"F17.opExtrude","SWEPT_BODY",BODY,{"disambiguationData":[OSD([sQuery(id+"F8.wireOp",EDGE,"E53"),sQuery(id+"F8.wireOp",EDGE,"E54"),sQuery(id+"F8.wireOp",EDGE,"E55"),sQuery(id+"F8.wireOp",EDGE,"E56.MirrorCS"),sQuery(id+"F8.wireOp",EDGE,"E57.MirrorCS"),sQuery(id+"F8.wireOp",EDGE,"E58.MirrorCS"),sQuery(id+"F8.wireOp",EDGE,"E59")])]});
            booleanBodies(context, id + "F18", {"operationType" : BooleanOperationType.INTERSECTION, "tools" : qUnion([Q0, Q1])});
        }
        {
            var Q0;
            Q0=makeQuery(id+"F9.imprint","IMPRINT",FACE,{"disambiguationData":[TD([[makeQuery(id+"F9.imprint","IMPRINT",EDGE,{"derivedFrom":sQuery(id+"F9.wireOp",EDGE,"E60")}),1.0]])]});
            var Q1;
            Q1=makeQuery(id+"F9.imprint","IMPRINT",FACE,{"disambiguationData":[TD([[makeQuery(id+"F9.imprint","IMPRINT",EDGE,{"derivedFrom":sQuery(id+"F9.wireOp",EDGE,"E68.bottom")}),-1.0]])]});
            var Q2;
            Q2=makeQuery(id+"F9.imprint","IMPRINT",FACE,{"disambiguationData":[TD([[makeQuery(id+"F9.imprint","IMPRINT",EDGE,{"derivedFrom":sQuery(id+"F9.wireOp",EDGE,"E67.bottom")}),1.0]])]});
            extrude(context, id + "F19", {"entities" : qUnion([Q0, Q1, Q2]), "depth" : 44.2 * mm, "offsetDistance" : 25.4 * mm});
        }
        {
            var Q0;
            Q0=makeQuery(id+"F8.imprint","IMPRINT",FACE,{"disambiguationData":[TD([[makeQuery(id+"F8.imprint","IMPRINT",EDGE,{"derivedFrom":sQuery(id+"F8.wireOp",EDGE,"E50.bottom")}),1.0]])]});
            extrude(context, id + "F20", {"entities" : qUnion([Q0]), "depth" : 86.36 * mm, "offsetDistance" : 25.4 * mm});
        }
        {
            var Q0;
            Q0=makeQuery(id+"F19.opExtrude","SWEPT_BODY",BODY,{"disambiguationData":[OSD([sQuery(id+"F9.wireOp",EDGE,"E60"),sQuery(id+"F9.wireOp",EDGE,"E61"),sQuery(id+"F9.wireOp",EDGE,"E62"),sQuery(id+"F9.wireOp",EDGE,"E63.MirrorCS"),sQuery(id+"F9.wireOp",EDGE,"E64.MirrorCS"),sQuery(id+"F9.wireOp",EDGE,"E65.MirrorCS"),sQuery(id+"F9.wireOp",EDGE,"E66")])]});
            var Q1;
            Q1=makeQuery(id+"F20.opExtrude","SWEPT_BODY",BODY,{"disambiguationData":[OSD([sQuery(id+"F8.wireOp",EDGE,"E50.bottom"),sQuery(id+"F8.wireOp",EDGE,"E50.top"),sQuery(id+"F8.wireOp",EDGE,"E50.left"),sQuery(id+"F8.wireOp",EDGE,"E50.right"),sQuery(id+"F8.wireOp",EDGE,"E51.bottom"),sQuery(id+"F8.wireOp",EDGE,"E51.top"),sQuery(id+"F8.wireOp",EDGE,"E51.left"),sQuery(id+"F8.wireOp",EDGE,"E51.right"),sQuery(id+"F8.wireOp",EDGE,"E52.bottom"),sQuery(id+"F8.wireOp",EDGE,"E52.top"),sQuery(id+"F8.wireOp",EDGE,"E52.left"),sQuery(id+"F8.wireOp",EDGE,"E52.right"),sQuery(id+"F8.wireOp",EDGE,"E53"),sQuery(id+"F8.wireOp",EDGE,"E54"),sQuery(id+"F8.wireOp",EDGE,"E55"),sQuery(id+"F8.wireOp",EDGE,"E56.MirrorCS"),sQuery(id+"F8.wireOp",EDGE,"E57.MirrorCS"),sQuery(id+"F8.wireOp",EDGE,"E58.MirrorCS"),sQuery(id+"F8.wireOp",EDGE,"E59")])]});
            booleanBodies(context, id + "F21", {"operationType" : BooleanOperationType.INTERSECTION, "tools" : qUnion([Q0, Q1])});
        }
        {
            var Q0;
            Q0=makeQuery(id+"F0.imprint","IMPRINT",FACE,{"disambiguationData":[TD([[makeQuery(id+"F0.imprint","IMPRINT",EDGE,{"derivedFrom":sQuery(id+"F0.wireOp",EDGE,"E0.bottom")}),1.0]])]});
            var Q1;
            Q1=makeQuery(id+"F0.imprint","IMPRINT",FACE,{"disambiguationData":[TD([[makeQuery(id+"F0.imprint","IMPRINT",EDGE,{"derivedFrom":sQuery(id+"F0.wireOp",EDGE,"E0.bottom")}),-1.0]])]});
            var Q2;
            Q2=makeQuery(id+"F0.imprint","IMPRINT",FACE,{"disambiguationData":[TD([[makeQuery(id+"F0.imprint","IMPRINT",EDGE,{"derivedFrom":sQuery(id+"F0.wireOp",EDGE,"E8.right")}),1.0]])]});
            extrude(context, id + "F22", {"entities" : qUnion([Q0, Q1, Q2]), "operationType" : NewBodyOperationType.REMOVE, "depth" : 66.04 * mm, "offsetDistance" : 25.4 * mm});
        }
        {
            var Q0;
            Q0=makeQuery(id+"F7.imprint","IMPRINT",FACE,{"disambiguationData":[TD([[makeQuery(id+"F7.imprint","IMPRINT",EDGE,{"derivedFrom":sQuery(id+"F7.wireOp",EDGE,"E49.bottom")}),-1.0]])]});
            extrude(context, id + "F23", {"entities" : qUnion([Q0]), "operationType" : NewBodyOperationType.REMOVE, "depth" : 61.72 * mm, "offsetDistance" : 25.4 * mm});
        }
        {
            var Q0;
            Q0=makeQuery(id+"F6.imprint","IMPRINT",FACE,{"disambiguationData":[TD([[makeQuery(id+"F6.imprint","IMPRINT",EDGE,{"derivedFrom":sQuery(id+"F6.wireOp",EDGE,"E48.bottom")}),-1.0]])]});
            var Q1;
            Q1=makeQuery(id+"F6.imprint","IMPRINT",FACE,{"disambiguationData":[TD([[makeQuery(id+"F6.imprint","IMPRINT",EDGE,{"derivedFrom":sQuery(id+"F6.wireOp",EDGE,"E47.bottom")}),1.0]])]});
            extrude(context, id + "F24", {"entities" : qUnion([Q0, Q1]), "operationType" : NewBodyOperationType.REMOVE, "oppositeDirection" : true, "depth" : 61.72 * mm, "offsetDistance" : 25.4 * mm});
        }
        {
            var Q0;
            Q0=qCreatedBy(makeId("Right.planeOp"),FACE);
            var sketch = newSketch(context, id + "F25", { "sketchPlane" : qUnion([Q0])});
            skLineSegment(sketch, "E69", {"start": v(-76.12, -66.83) * mm, "end": v(76.42, -63.68) * mm});
            skLineSegment(sketch, "E70", {"start": v(0, -32.67) * mm, "end": v(-51.93, -32.67) * mm});
            skLineSegment(sketch, "E71", {"start": v(-76.12, -87.62) * mm, "end": v(76.42, -84.47) * mm});
            skLineSegment(sketch, "E72", {"start": v(-76.12, -66.83) * mm, "end": v(-76.12, -87.62) * mm});
            skLineSegment(sketch, "E73", {"start": v(76.42, -63.68) * mm, "end": v(76.42, -84.47) * mm});
            skSolve(sketch);
        }
        {
            var Q0;
            Q0=makeQuery(id+"F25.imprint","IMPRINT",FACE,{"disambiguationData":[TD([[makeQuery(id+"F25.imprint","IMPRINT",EDGE,{"derivedFrom":sQuery(id+"F25.wireOp",EDGE,"E69")}),-1.0]])]});
            var Q1;
            Q1=sQuery(id+"F25.wireOp",EDGE,"E70");
            revolve(context, id + "F26", {"entities" : qUnion([Q0]), "axis" : qUnion([Q1]), "revolveType" : RevolveType.FULL});
        }
        {
            var Q0;
            Q0=qCreatedBy(makeId("Right.planeOp"),FACE);
            var sketch = newSketch(context, id + "F27", { "sketchPlane" : qUnion([Q0])});
            skLineSegment(sketch, "E74.bottom", {"start": v(-79.27, 0) * mm, "end": v(79.16, 0) * mm});
            skLineSegment(sketch, "E74.top", {"start": v(-79.27, 31.31) * mm, "end": v(79.16, 31.31) * mm});
            skLineSegment(sketch, "E74.left", {"start": v(-79.27, 0) * mm, "end": v(-79.27, 31.31) * mm});
            skLineSegment(sketch, "E74.right", {"start": v(79.16, 0) * mm, "end": v(79.16, 31.31) * mm});
            skSolve(sketch);
        }
        {
            var Q0;
            Q0=makeQuery(id+"F27.imprint","IMPRINT",FACE,{"disambiguationData":[TD([[makeQuery(id+"F27.imprint","IMPRINT",EDGE,{"derivedFrom":sQuery(id+"F27.wireOp",EDGE,"E74.bottom")}),1.0]])]});
            extrude(context, id + "F28", {"entities" : qUnion([Q0]), "operationType" : NewBodyOperationType.REMOVE, "oppositeDirection" : true, "depth" : 39.37 * mm, "offsetDistance" : 25.4 * mm, "hasSecondDirection" : true, "secondDirectionOppositeDirection" : false, "secondDirectionDepth" : 39.62 * mm});
        }
    });
